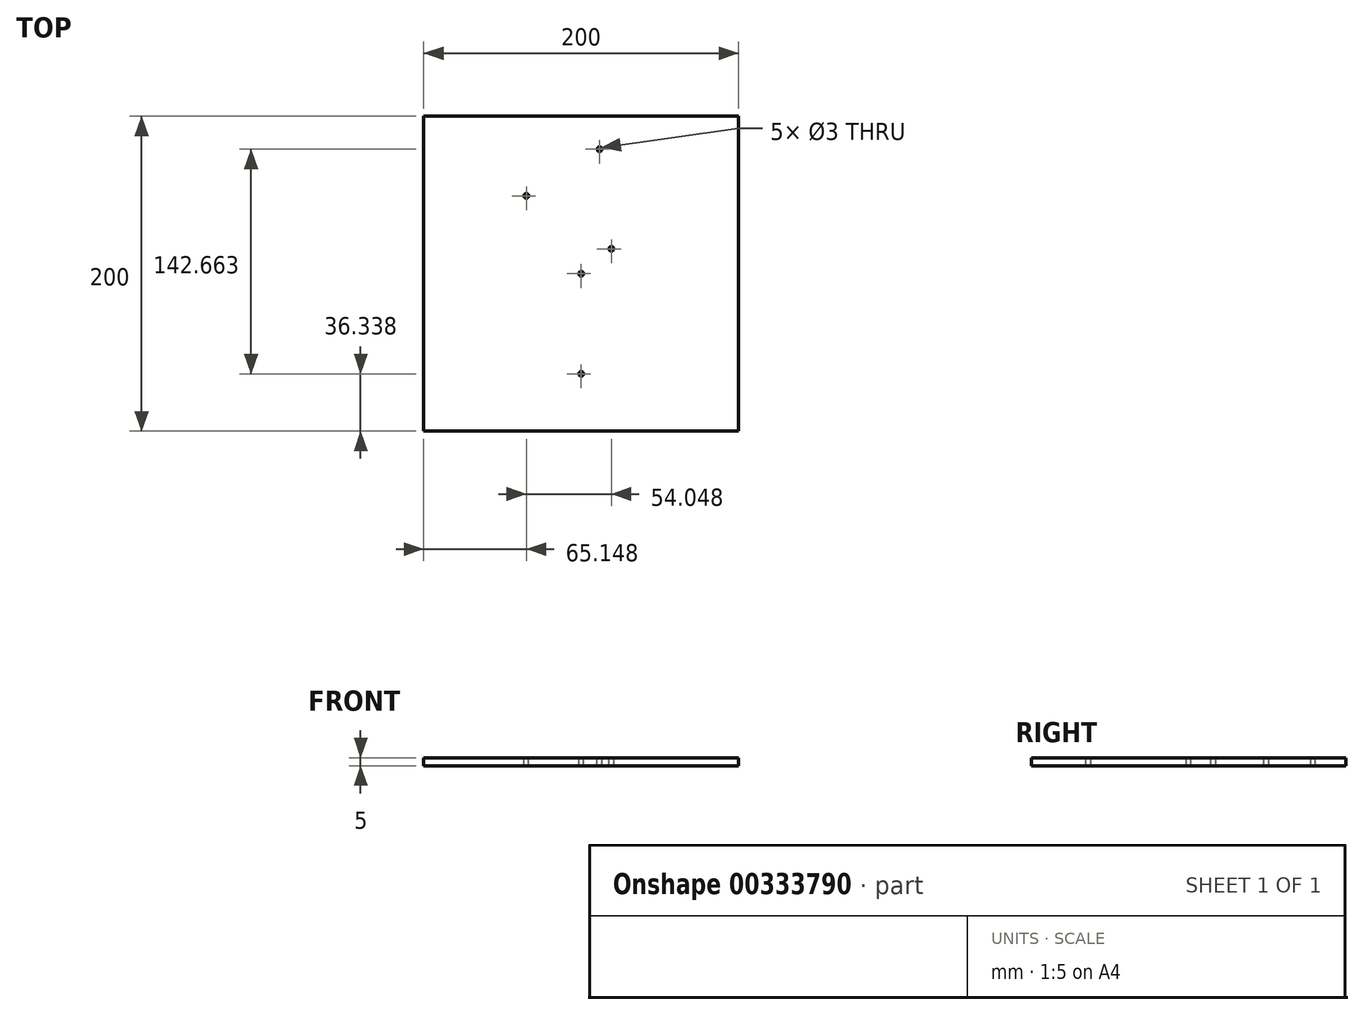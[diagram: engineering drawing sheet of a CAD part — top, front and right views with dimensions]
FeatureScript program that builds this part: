
annotation { "Feature Type Name" : "Feature", "Feature Type Description" : "" }
export const myFeature = defineFeature(function(context is Context, id is Id, definition is map)
    precondition{}
    {
        {
            var Q0;
            Q0=qCreatedBy(makeId("Top.planeOp"),FACE);
            var sketch = newSketch(context, id + "F0", { "sketchPlane" : qUnion([Q0])});
            skLineSegment(sketch, "E0.bottom", {"start": v(100, 100) * mm, "end": v(-100, 100) * mm});
            skLineSegment(sketch, "E0.top", {"start": v(100, -100) * mm, "end": v(-100, -100) * mm});
            skLineSegment(sketch, "E0.left", {"start": v(100, 100) * mm, "end": v(100, -100) * mm});
            skLineSegment(sketch, "E0.right", {"start": v(-100, 100) * mm, "end": v(-100, -100) * mm});
            skPoint(sketch, "E0.middle", {"position": v(0, 0) * mm});
            skSolve(sketch);
        }
        {
            var Q0;
            Q0 = qSketchRegion(id + "F0", true);
            extrude(context, id + "F1", {"entities" : qUnion([Q0]), "depth" : 5 * mm});
        }
        {
            var Q0;
            Q0=makeQuery(id+"F1.opExtrude","CAP_FACE",FACE,{"disambiguationData":[OSD([sQuery(id+"F0.wireOp",EDGE,"E0.bottom"),sQuery(id+"F0.wireOp",EDGE,"E0.top"),sQuery(id+"F0.wireOp",EDGE,"E0.left"),sQuery(id+"F0.wireOp",EDGE,"E0.right")])],"isStart":false});
            var sketch = newSketch(context, id + "F2", { "sketchPlane" : qUnion([Q0])});
            skCircle(sketch, "E1", {"center": v(0, 0) * mm, "radius": 1.5 * mm});
            skCircle(sketch, "E2", {"center": v(0, -63.66) * mm, "radius": 1.5 * mm});
            skCircle(sketch, "E3", {"center": v(11.66, 79) * mm, "radius": 1.5 * mm});
            skCircle(sketch, "E4", {"center": v(-34.85, 49.43) * mm, "radius": 1.5 * mm});
            skCircle(sketch, "E5", {"center": v(19.2, 15.79) * mm, "radius": 1.5 * mm});
            skSolve(sketch);
        }
        {
            var Q0;
            Q0 = qSketchRegion(id + "F2", true);
            extrude(context, id + "F3", {"entities" : qUnion([Q0]), "operationType" : NewBodyOperationType.REMOVE, "endBound" : BoundingType.THROUGH_ALL, "oppositeDirection" : true, "depth" : 25 * mm});
        }
    });
